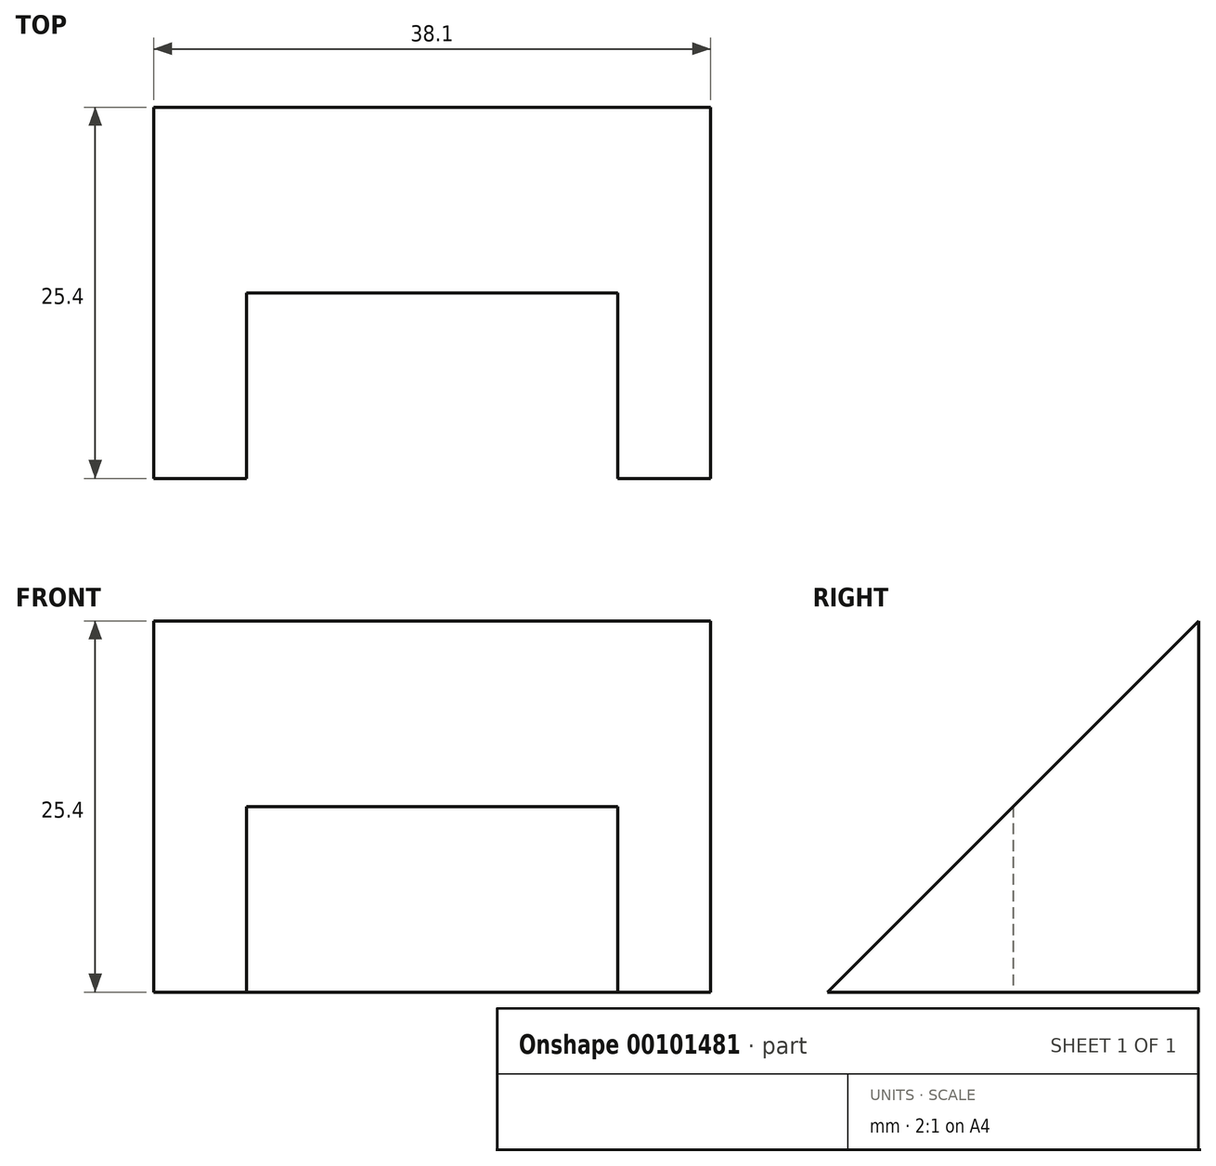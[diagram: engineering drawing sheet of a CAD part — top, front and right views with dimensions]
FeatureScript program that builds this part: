
annotation { "Feature Type Name" : "Feature", "Feature Type Description" : "" }
export const myFeature = defineFeature(function(context is Context, id is Id, definition is map)
    precondition{}
    {
        {
            var Q0;
            Q0=qCreatedBy(makeId("Right.planeOp"),FACE);
            var sketch = newSketch(context, id + "F0", { "sketchPlane" : qUnion([Q0])});
            skLineSegment(sketch, "E0", {"start": v(0, 0) * mm, "end": v(0, 25.4) * mm});
            skLineSegment(sketch, "E1", {"start": v(0, 25.4) * mm, "end": v(-25.4, 0) * mm});
            skLineSegment(sketch, "E2", {"start": v(-25.4, 0) * mm, "end": v(0, 0) * mm});
            skSolve(sketch);
        }
        {
            var Q0;
            Q0 = qSketchRegion(id + "F0", true);
            extrude(context, id + "F1", {"entities" : qUnion([Q0]), "endBound" : BoundingType.SYMMETRIC, "depth" : 38.1 * mm});
        }
        {
            var Q0;
            Q0=qCreatedBy(makeId("Right.planeOp"),FACE);
            var sketch = newSketch(context, id + "F2", { "sketchPlane" : qUnion([Q0])});
            skLineSegment(sketch, "E3", {"start": v(-12.7, 0) * mm, "end": v(-25.4, 0) * mm});
            skLineSegment(sketch, "E4", {"start": v(-25.4, 0) * mm, "end": v(-12.7, 12.7) * mm});
            skLineSegment(sketch, "E5", {"start": v(-12.7, 12.7) * mm, "end": v(-12.7, 0) * mm});
            skSolve(sketch);
        }
        {
            var Q0;
            Q0 = qSketchRegion(id + "F2", true);
            extrude(context, id + "F3", {"entities" : qUnion([Q0]), "operationType" : NewBodyOperationType.REMOVE, "endBound" : BoundingType.SYMMETRIC, "depth" : 25.4 * mm});
        }
    });
